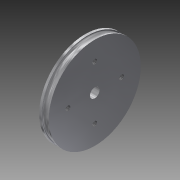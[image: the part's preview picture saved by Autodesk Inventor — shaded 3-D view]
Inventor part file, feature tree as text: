
AUTODESK INVENTOR PART (.ipt)
format: ipt  version: 2015 (Build 190159000, 159)  size: 144,896 bytes
history: native  units: mm
features: sketch x3, hole x2, other x1, revolve x1
ambient origin geometry x8: Origin, YZ Plane, XZ Plane, XY Plane, X Axis, Y Axis, Z Axis, Center Point
bodies: Body1 (feature_tree)
feature tree (7):
  other  "ソリッド1"
  revolve  "回転1"
  hole  "穴1"  [1 undecoded]
  hole  "穴2"  [1 undecoded]
  sketch  "スケッチ1"
  sketch  "スケッチ2"
  sketch  "スケッチ3"
note: 2 required parameter values undecoded (feature->parameter linkage not recoverable at this tier; creation-order binding heuristic only, values carry confidence <= 0.55)
